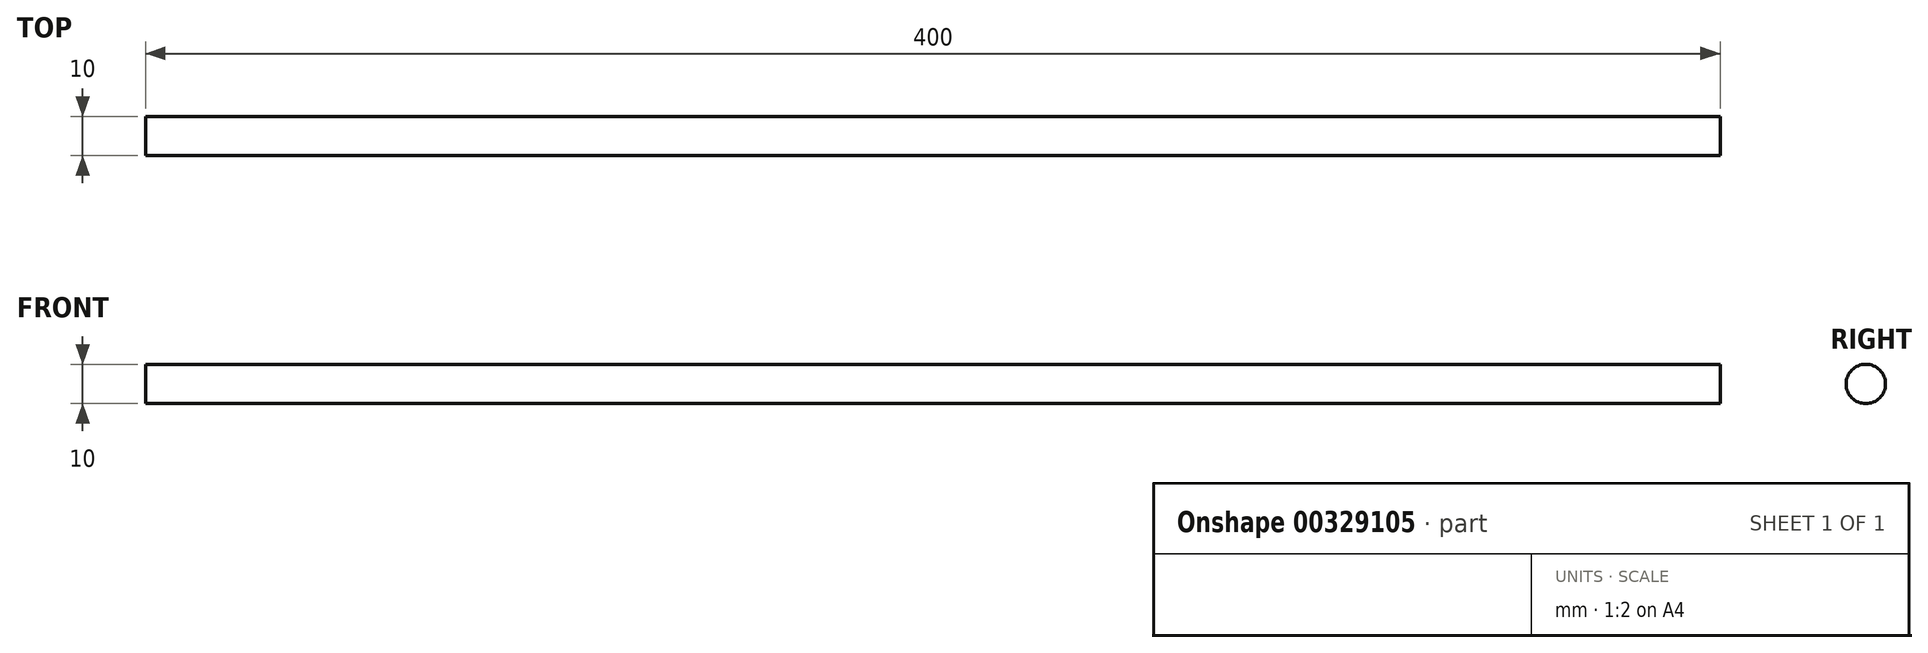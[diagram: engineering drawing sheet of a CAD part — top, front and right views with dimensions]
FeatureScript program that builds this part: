
annotation { "Feature Type Name" : "Feature", "Feature Type Description" : "" }
export const myFeature = defineFeature(function(context is Context, id is Id, definition is map)
    precondition{}
    {
        {
            var Q0;
            Q0=qCreatedBy(makeId("Right.planeOp"),FACE);
            var sketch = newSketch(context, id + "F0", { "sketchPlane" : qUnion([Q0])});
            skCircle(sketch, "E0", {"center": v(0, 0) * mm, "radius": 5 * mm});
            skSolve(sketch);
        }
        {
            var Q0;
            Q0 = qSketchRegion(id + "F0", true);
            extrude(context, id + "F1", {"entities" : qUnion([Q0]), "depth" : 400 * mm});
        }
    });
